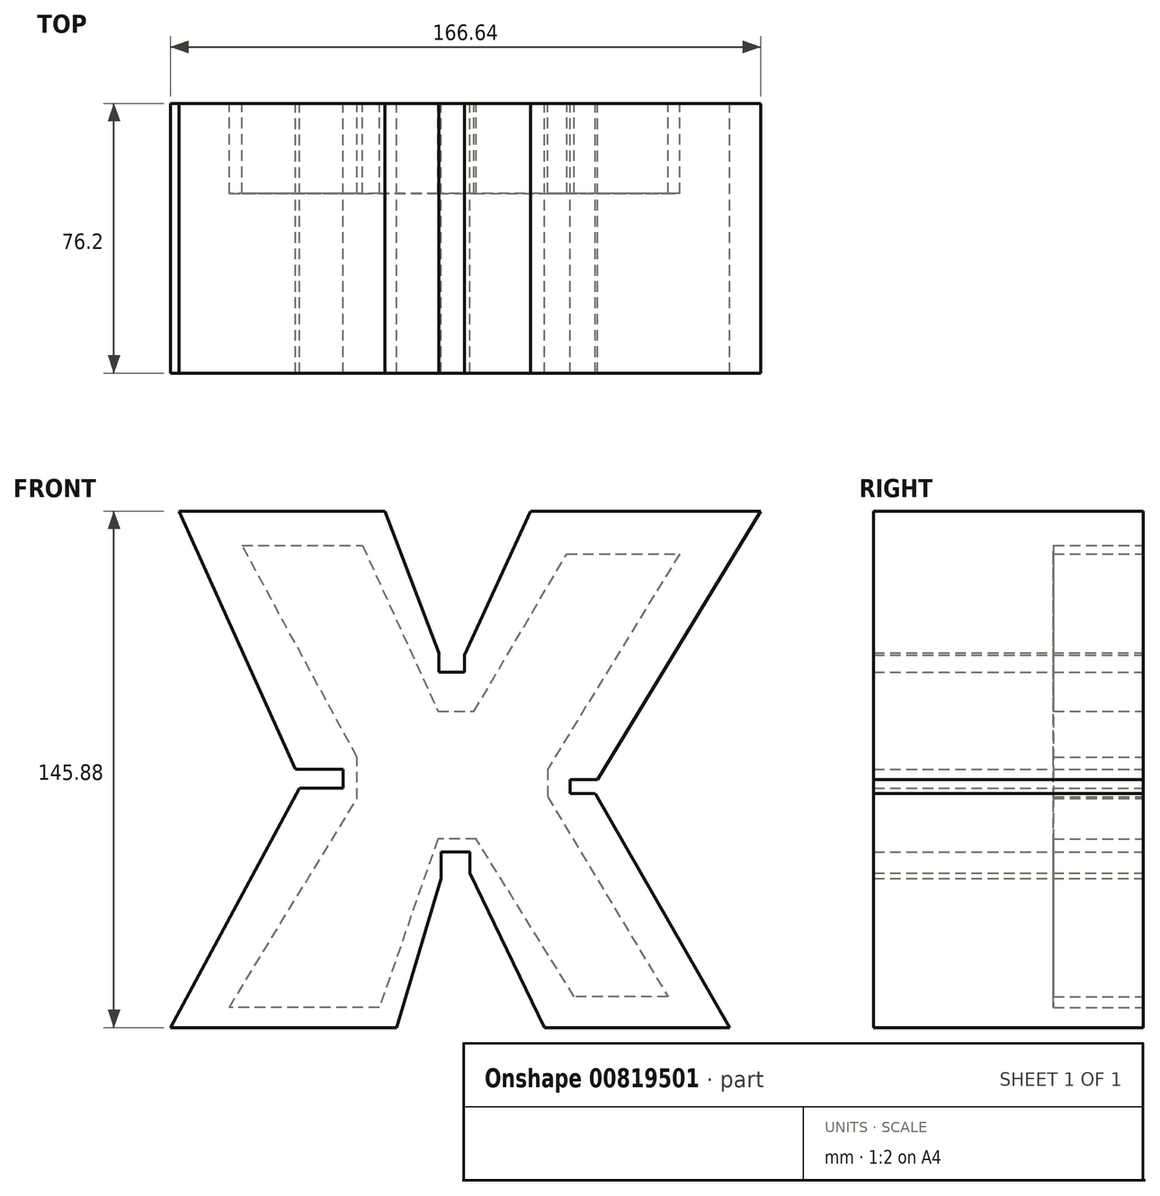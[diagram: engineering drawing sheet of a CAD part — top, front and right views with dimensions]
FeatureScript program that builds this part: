
annotation { "Feature Type Name" : "Feature", "Feature Type Description" : "" }
export const myFeature = defineFeature(function(context is Context, id is Id, definition is map)
    precondition{}
    {
        {
            var Q0;
            Q0=qCreatedBy(makeId("Front.planeOp"),FACE);
            var sketch = newSketch(context, id + "F0", { "sketchPlane" : qUnion([Q0])});
            skPoint(sketch, "E0.middle", {"position": v(0, 0) * mm});
            skLineSegment(sketch, "E1", {"start": v(-76.85, 72.94) * mm, "end": v(-44.07, 0) * mm});
            skLineSegment(sketch, "E2", {"start": v(-44.07, 0) * mm, "end": v(-30.53, 0) * mm});
            skLineSegment(sketch, "E3", {"start": v(-30.53, 0) * mm, "end": v(-30.53, -5.26) * mm});
            skLineSegment(sketch, "E4", {"start": v(-30.53, -5.26) * mm, "end": v(-42.86, -5.26) * mm});
            skLineSegment(sketch, "E5", {"start": v(-42.86, -5.26) * mm, "end": v(-79.26, -72.94) * mm});
            skLineSegment(sketch, "E6", {"start": v(-79.26, -72.94) * mm, "end": v(-15.5, -72.94) * mm});
            skLineSegment(sketch, "E7", {"start": v(-15.5, -72.94) * mm, "end": v(-2.86, -30.83) * mm});
            skLineSegment(sketch, "E8", {"start": v(-2.86, -30.83) * mm, "end": v(-2.86, -23.31) * mm});
            skLineSegment(sketch, "E9", {"start": v(-2.86, -23.31) * mm, "end": v(5.26, -23.31) * mm});
            skLineSegment(sketch, "E10", {"start": v(5.26, -23.31) * mm, "end": v(5.26, -29.33) * mm});
            skLineSegment(sketch, "E11", {"start": v(5.26, -29.33) * mm, "end": v(26.32, -72.94) * mm});
            skLineSegment(sketch, "E12", {"start": v(26.32, -72.94) * mm, "end": v(78.66, -72.94) * mm});
            skLineSegment(sketch, "E13", {"start": v(78.66, -72.94) * mm, "end": v(40.76, -6.77) * mm});
            skLineSegment(sketch, "E14", {"start": v(40.76, -6.77) * mm, "end": v(33.54, -6.77) * mm});
            skLineSegment(sketch, "E15", {"start": v(33.54, -6.77) * mm, "end": v(33.54, -2.86) * mm});
            skLineSegment(sketch, "E16", {"start": v(33.54, -2.86) * mm, "end": v(41.36, -2.86) * mm});
            skLineSegment(sketch, "E17", {"start": v(41.36, -2.86) * mm, "end": v(87.38, 72.94) * mm});
            skLineSegment(sketch, "E18", {"start": v(87.38, 72.94) * mm, "end": v(22.4, 72.94) * mm});
            skLineSegment(sketch, "E19", {"start": v(22.4, 72.94) * mm, "end": v(3.76, 32.33) * mm});
            skLineSegment(sketch, "E20", {"start": v(3.76, 32.33) * mm, "end": v(3.76, 27.52) * mm});
            skLineSegment(sketch, "E21", {"start": v(3.76, 27.52) * mm, "end": v(-3.46, 27.52) * mm});
            skLineSegment(sketch, "E22", {"start": v(-3.46, 27.52) * mm, "end": v(-3.46, 32.94) * mm});
            skLineSegment(sketch, "E23", {"start": v(-3.46, 32.94) * mm, "end": v(-18.8, 72.94) * mm});
            skLineSegment(sketch, "E24", {"start": v(-18.8, 72.94) * mm, "end": v(-76.85, 72.94) * mm});
            skSolve(sketch);
        }
        {
            var Q0;
            Q0=qCreatedBy(makeId("Front.planeOp"),FACE);
            var sketch = newSketch(context, id + "F1", { "sketchPlane" : qUnion([Q0])});
            skLineSegment(sketch, "E25", {"start": v(-59.1, 63.32) * mm, "end": v(-25.12, 63.32) * mm});
            skLineSegment(sketch, "E26", {"start": v(-25.12, 63.32) * mm, "end": v(-3.76, 16.4) * mm});
            skLineSegment(sketch, "E27", {"start": v(-3.76, 16.4) * mm, "end": v(6.47, 16.4) * mm});
            skLineSegment(sketch, "E28", {"start": v(6.47, 16.4) * mm, "end": v(32.64, 60.9) * mm});
            skLineSegment(sketch, "E29", {"start": v(32.64, 60.9) * mm, "end": v(64.52, 60.9) * mm});
            skLineSegment(sketch, "E30", {"start": v(64.52, 60.9) * mm, "end": v(27.22, 0) * mm});
            skLineSegment(sketch, "E31", {"start": v(27.22, 0) * mm, "end": v(27.22, -7.67) * mm});
            skLineSegment(sketch, "E32", {"start": v(27.22, -7.67) * mm, "end": v(61.21, -64.22) * mm});
            skLineSegment(sketch, "E33", {"start": v(61.21, -64.22) * mm, "end": v(34.74, -64.22) * mm});
            skLineSegment(sketch, "E34", {"start": v(34.74, -64.22) * mm, "end": v(7.07, -19.7) * mm});
            skLineSegment(sketch, "E35", {"start": v(7.07, -19.7) * mm, "end": v(-3.76, -19.7) * mm});
            skLineSegment(sketch, "E36", {"start": v(-3.76, -19.7) * mm, "end": v(-20.3, -67.23) * mm});
            skLineSegment(sketch, "E37", {"start": v(-20.3, -67.23) * mm, "end": v(-62.71, -67.23) * mm});
            skLineSegment(sketch, "E38", {"start": v(-62.71, -67.23) * mm, "end": v(-26.62, -8.27) * mm});
            skLineSegment(sketch, "E39", {"start": v(-26.62, -8.27) * mm, "end": v(-26.62, 3.46) * mm});
            skLineSegment(sketch, "E40", {"start": v(-26.62, 3.46) * mm, "end": v(-59.1, 63.32) * mm});
            skSolve(sketch);
        }
        {
            var Q0;
            Q0 = qSketchRegion(id + "F0", true);
            extrude(context, id + "F2", {"entities" : qUnion([Q0]), "depth" : 76.2 * mm, "offsetDistance" : 25.4 * mm});
        }
        {
            var Q0;
            Q0 = qSketchRegion(id + "F1", true);
            extrude(context, id + "F3", {"entities" : qUnion([Q0]), "operationType" : NewBodyOperationType.REMOVE, "depth" : 25.4 * mm, "offsetDistance" : 25.4 * mm});
        }
    });
